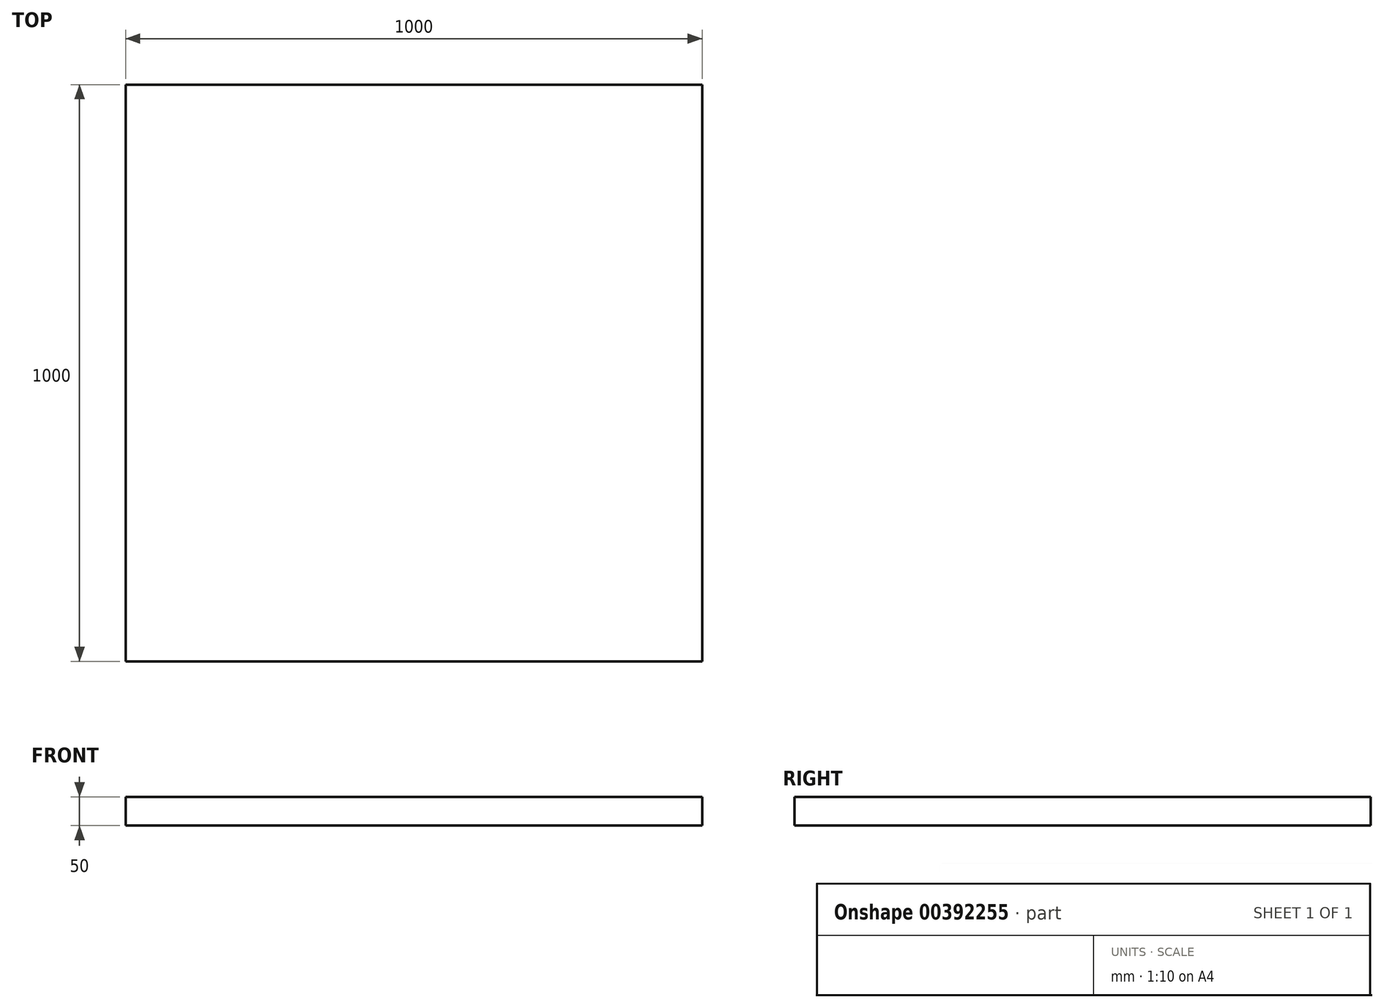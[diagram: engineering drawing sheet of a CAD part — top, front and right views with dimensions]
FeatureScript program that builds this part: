
annotation { "Feature Type Name" : "Feature", "Feature Type Description" : "" }
export const myFeature = defineFeature(function(context is Context, id is Id, definition is map)
    precondition{}
    {
        {
            var Q0;
            Q0=qCreatedBy(makeId("Top.planeOp"),FACE);
            var sketch = newSketch(context, id + "F0", { "sketchPlane" : qUnion([Q0])});
            skLineSegment(sketch, "E0.bottom", {"start": v(500, 500) * mm, "end": v(-500, 500) * mm});
            skLineSegment(sketch, "E0.top", {"start": v(500, -500) * mm, "end": v(-500, -500) * mm});
            skLineSegment(sketch, "E0.left", {"start": v(500, 500) * mm, "end": v(500, -500) * mm});
            skLineSegment(sketch, "E0.right", {"start": v(-500, 500) * mm, "end": v(-500, -500) * mm});
            skPoint(sketch, "E0.middle", {"position": v(0, 0) * mm});
            skSolve(sketch);
        }
        {
            var Q0;
            Q0 = qSketchRegion(id + "F0", true);
            extrude(context, id + "F1", {"entities" : qUnion([Q0]), "depth" : 50 * mm, "offsetDistance" : 25 * mm});
        }
    });
